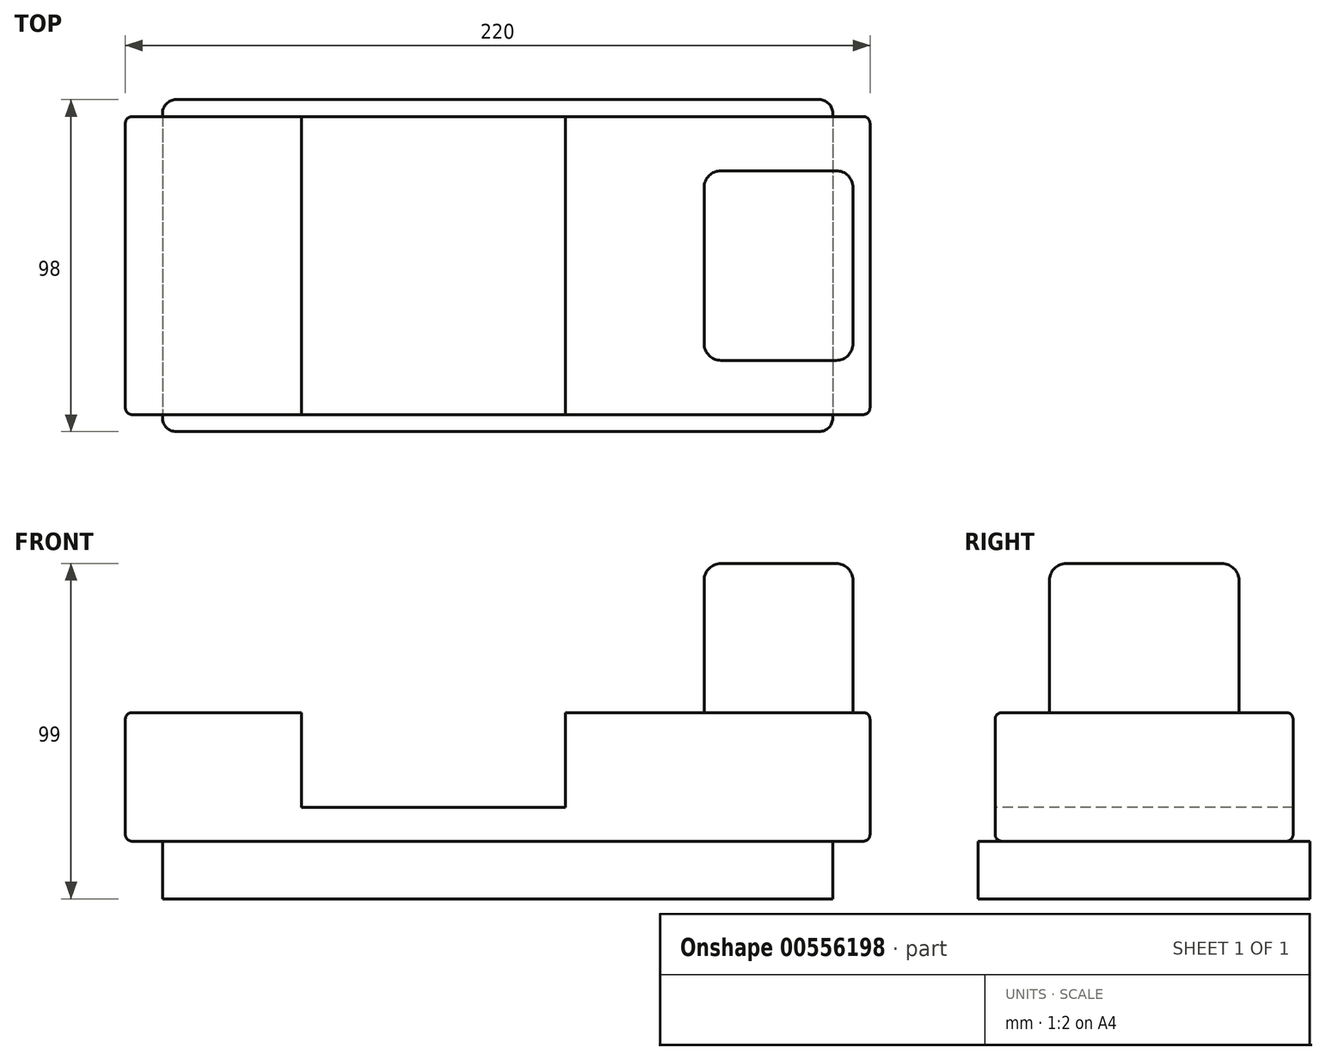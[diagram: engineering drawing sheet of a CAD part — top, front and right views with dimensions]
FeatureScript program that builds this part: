
annotation { "Feature Type Name" : "Feature", "Feature Type Description" : "" }
export const myFeature = defineFeature(function(context is Context, id is Id, definition is map)
    precondition{}
    {
        {
            assignVariable(context, id + "F0", {"name" : "cutdepth", "anyValue" : 28});
        }
        {
            var Q0;
            Q0=qCreatedBy(makeId("Top.planeOp"),FACE);
            var sketch = newSketch(context, id + "F1", { "sketchPlane" : qUnion([Q0])});
            skLineSegment(sketch, "E0.bottom", {"start": v(-89, 44.19) * mm, "end": v(109, 44.19) * mm});
            skLineSegment(sketch, "E0.top", {"start": v(-89, -53.81) * mm, "end": v(109, -53.81) * mm});
            skLineSegment(sketch, "E0.left", {"start": v(-89, 44.19) * mm, "end": v(-89, -53.81) * mm});
            skLineSegment(sketch, "E0.right", {"start": v(109, 44.19) * mm, "end": v(109, -53.81) * mm});
            skSolve(sketch);
        }
        {
            var Q0;
            Q0=qSketchRegion(id+"F1",true);
            extrude(context, id + "F2", {"entities" : qUnion([Q0]), "depth" : 17 * mm});
        }
        {
            var Q0;
            Q0=makeQuery(id+"F2.opExtrude","CAP_FACE",FACE,{"disambiguationData":[OSD([sQuery(id+"F1.wireOp",EDGE,"E0.bottom"),sQuery(id+"F1.wireOp",EDGE,"E0.top"),sQuery(id+"F1.wireOp",EDGE,"E0.left"),sQuery(id+"F1.wireOp",EDGE,"E0.right")])],"isStart":false});
            var sketch = newSketch(context, id + "F3", { "sketchPlane" : qUnion([Q0])});
            skLineSegment(sketch, "E1.bottom", {"start": v(-100, 39.19) * mm, "end": v(120, 39.19) * mm});
            skLineSegment(sketch, "E1.top", {"start": v(-100, -48.81) * mm, "end": v(120, -48.81) * mm});
            skLineSegment(sketch, "E1.left", {"start": v(-100, 39.19) * mm, "end": v(-100, -48.81) * mm});
            skLineSegment(sketch, "E1.right", {"start": v(120, 39.19) * mm, "end": v(120, -48.81) * mm});
            skLineSegment(sketch, "E2", {"start": v(10, -53.81) * mm, "end": v(10, 44.19) * mm, "construction": true});
            skLineSegment(sketch, "E3", {"start": v(-89, -4.81) * mm, "end": v(109, -4.81) * mm, "construction": true});
            skLineSegment(sketch, "E4", {"start": v(120, -48.81) * mm, "end": v(-100, 39.19) * mm, "construction": true});
            skLineSegment(sketch, "E5", {"start": v(-100, -48.81) * mm, "end": v(120, 39.19) * mm, "construction": true});
            skPoint(sketch, "E6", {"position": v(10, -4.81) * mm});
            skSolve(sketch);
        }
        {
            var Q0;
            Q0=qSketchRegion(id+"F3",true);
            extrude(context, id + "F4", {"entities" : qUnion([Q0]), "depth" : 38 * mm});
        }
        {
            var Q0;
            Q0=makeQuery(id+"F4.opExtrude","CAP_FACE",FACE,{"disambiguationData":[OSD([sQuery(id+"F3.wireOp",EDGE,"E1.bottom"),sQuery(id+"F3.wireOp",EDGE,"E1.top"),sQuery(id+"F3.wireOp",EDGE,"E1.left"),sQuery(id+"F3.wireOp",EDGE,"E1.right")])],"isStart":false});
            var sketch = newSketch(context, id + "F5", { "sketchPlane" : qUnion([Q0])});
            skLineSegment(sketch, "E7", {"start": v(93, 39.19) * mm, "end": v(93, -48.81) * mm, "construction": true});
            skPoint(sketch, "E8", {"position": v(93, -4.81) * mm});
            skLineSegment(sketch, "E9.bottom", {"start": v(115, 23.19) * mm, "end": v(71, 23.19) * mm});
            skLineSegment(sketch, "E9.top", {"start": v(115, -32.81) * mm, "end": v(71, -32.81) * mm});
            skLineSegment(sketch, "E9.left", {"start": v(115, 23.19) * mm, "end": v(115, -32.81) * mm});
            skLineSegment(sketch, "E9.right", {"start": v(71, 23.19) * mm, "end": v(71, -32.81) * mm});
            skLineSegment(sketch, "E10", {"start": v(115, 23.19) * mm, "end": v(71, -32.81) * mm, "construction": true});
            skSolve(sketch);
        }
        {
            var Q0;
            Q0=qSketchRegion(id+"F5",true);
            extrude(context, id + "F6", {"entities" : qUnion([Q0]), "depth" : 44 * mm});
        }
        {
            var Q0;
            Q0=makeQuery(id+"F4.opExtrude","CAP_FACE",FACE,{"disambiguationData":[OSD([sQuery(id+"F3.wireOp",EDGE,"E1.bottom"),sQuery(id+"F3.wireOp",EDGE,"E1.top"),sQuery(id+"F3.wireOp",EDGE,"E1.left"),sQuery(id+"F3.wireOp",EDGE,"E1.right")])],"isStart":false});
            var sketch = newSketch(context, id + "F7", { "sketchPlane" : qUnion([Q0])});
            skLineSegment(sketch, "E11.bottom", {"start": v(-48, 40.7) * mm, "end": v(30, 40.7) * mm});
            skLineSegment(sketch, "E11.top", {"start": v(-48, -49.3) * mm, "end": v(30, -49.3) * mm});
            skLineSegment(sketch, "E11.left", {"start": v(-48, 40.7) * mm, "end": v(-48, -49.3) * mm});
            skLineSegment(sketch, "E11.right", {"start": v(30, 40.7) * mm, "end": v(30, -49.3) * mm});
            skSolve(sketch);
        }
        {
            var Q0;
            Q0=qSketchRegion(id+"F7",true);
            extrude(context, id + "F8", {"entities" : qUnion([Q0]), "operationType" : NewBodyOperationType.REMOVE, "oppositeDirection" : true, "depth" : getVariable(context, 'cutdepth') * mm});
        }
        {
            var Q0;
            {var subQ0=sQuery(id+"F3.wireOp",EDGE,"E1.top");var subQ1=sQuery(id+"F3.wireOp",EDGE,"E1.left");Q0=makeQuery(id+"F8.boolean.opBoolean","SPLIT",EDGE,{"disambiguationData":[TD([makeQuery(id+"F4.opExtrude","SWEPT_FACE",FACE,{"disambiguationData":[OSD([subQ1])]})])],"derivedFrom":makeQuery(id+"F4.opExtrude","CAP_EDGE",EDGE,{"disambiguationData":[OSD([subQ0])],"isStart":false})});}
            var Q1;
            {var subQ0=sQuery(id+"F3.wireOp",EDGE,"E1.bottom");var subQ1=sQuery(id+"F3.wireOp",EDGE,"E1.left");Q1=makeQuery(id+"F8.boolean.opBoolean","SPLIT",EDGE,{"disambiguationData":[TD([makeQuery(id+"F4.opExtrude","SWEPT_FACE",FACE,{"disambiguationData":[OSD([subQ1])]})])],"derivedFrom":makeQuery(id+"F4.opExtrude","CAP_EDGE",EDGE,{"disambiguationData":[OSD([subQ0])],"isStart":false})});}
            var Q2;
            {var subQ0=sQuery(id+"F3.wireOp",EDGE,"E1.top");var subQ1=sQuery(id+"F3.wireOp",EDGE,"E1.right");Q2=makeQuery(id+"F8.boolean.opBoolean","SPLIT",EDGE,{"disambiguationData":[TD([makeQuery(id+"F4.opExtrude","SWEPT_FACE",FACE,{"disambiguationData":[OSD([subQ1])]})])],"derivedFrom":makeQuery(id+"F4.opExtrude","CAP_EDGE",EDGE,{"disambiguationData":[OSD([subQ0])],"isStart":false})});}
            var Q3;
            Q3=makeQuery(id+"F4.opExtrude","CAP_EDGE",EDGE,{"disambiguationData":[OSD([sQuery(id+"F3.wireOp",EDGE,"E1.top")])],"isStart":true});
            var Q4;
            {var subQ0=sQuery(id+"F3.wireOp",EDGE,"E1.bottom");var subQ1=sQuery(id+"F3.wireOp",EDGE,"E1.right");Q4=makeQuery(id+"F8.boolean.opBoolean","SPLIT",EDGE,{"disambiguationData":[TD([makeQuery(id+"F4.opExtrude","SWEPT_FACE",FACE,{"disambiguationData":[OSD([subQ1])]})])],"derivedFrom":makeQuery(id+"F4.opExtrude","CAP_EDGE",EDGE,{"disambiguationData":[OSD([subQ0])],"isStart":false})});}
            var Q5;
            Q5=makeQuery(id+"F4.opExtrude","CAP_EDGE",EDGE,{"disambiguationData":[OSD([sQuery(id+"F3.wireOp",EDGE,"E1.bottom")])],"isStart":true});
            var Q6;
            Q6=makeQuery(id+"F4.opExtrude","CAP_EDGE",EDGE,{"disambiguationData":[OSD([sQuery(id+"F3.wireOp",EDGE,"E1.left")])],"isStart":false});
            var Q7;
            Q7=makeQuery(id+"F4.opExtrude","SWEPT_EDGE",EDGE,{"disambiguationData":[OSD([sQuery(id+"F3.wireOp",EDGE,"E1.top"),sQuery(id+"F3.wireOp",EDGE,"E1.left")])]});
            var Q8;
            Q8=makeQuery(id+"F4.opExtrude","CAP_EDGE",EDGE,{"disambiguationData":[OSD([sQuery(id+"F3.wireOp",EDGE,"E1.left")])],"isStart":true});
            var Q9;
            Q9=makeQuery(id+"F4.opExtrude","SWEPT_EDGE",EDGE,{"disambiguationData":[OSD([sQuery(id+"F3.wireOp",EDGE,"E1.bottom"),sQuery(id+"F3.wireOp",EDGE,"E1.left")])]});
            var Q10;
            Q10=makeQuery(id+"F4.opExtrude","SWEPT_EDGE",EDGE,{"disambiguationData":[OSD([sQuery(id+"F3.wireOp",EDGE,"E1.top"),sQuery(id+"F3.wireOp",EDGE,"E1.right")])]});
            var Q11;
            Q11=makeQuery(id+"F4.opExtrude","CAP_EDGE",EDGE,{"disambiguationData":[OSD([sQuery(id+"F3.wireOp",EDGE,"E1.right")])],"isStart":false});
            var Q12;
            Q12=makeQuery(id+"F4.opExtrude","CAP_EDGE",EDGE,{"disambiguationData":[OSD([sQuery(id+"F3.wireOp",EDGE,"E1.right")])],"isStart":true});
            var Q13;
            Q13=makeQuery(id+"F4.opExtrude","SWEPT_EDGE",EDGE,{"disambiguationData":[OSD([sQuery(id+"F3.wireOp",EDGE,"E1.bottom"),sQuery(id+"F3.wireOp",EDGE,"E1.right")])]});
            var Q14;
            Q14=qNothing();
            fillet(context, id + "F9", {"entities" : qUnion([Q0, Q1, Q2, Q3, Q4, Q5, Q6, Q7, Q8, Q9, Q10, Q11, Q12, Q13, Q14]), "radius" : 2 * mm, "tangentPropagation" : true, "allowEdgeOverflow" : false});
        }
        {
            var Q0;
            Q0=makeQuery(id+"F2.opExtrude","SWEPT_EDGE",EDGE,{"disambiguationData":[OSD([sQuery(id+"F1.wireOp",EDGE,"E0.top"),sQuery(id+"F1.wireOp",EDGE,"E0.left")])]});
            var Q1;
            Q1=makeQuery(id+"F2.opExtrude","SWEPT_EDGE",EDGE,{"disambiguationData":[OSD([sQuery(id+"F1.wireOp",EDGE,"E0.top"),sQuery(id+"F1.wireOp",EDGE,"E0.right")])]});
            var Q2;
            Q2=makeQuery(id+"F2.opExtrude","SWEPT_EDGE",EDGE,{"disambiguationData":[OSD([sQuery(id+"F1.wireOp",EDGE,"E0.bottom"),sQuery(id+"F1.wireOp",EDGE,"E0.right")])]});
            var Q3;
            Q3=makeQuery(id+"F2.opExtrude","SWEPT_EDGE",EDGE,{"disambiguationData":[OSD([sQuery(id+"F1.wireOp",EDGE,"E0.bottom"),sQuery(id+"F1.wireOp",EDGE,"E0.left")])]});
            fillet(context, id + "F10", {"entities" : qUnion([Q0, Q1, Q2, Q3]), "radius" : 4 * mm, "tangentPropagation" : true, "allowEdgeOverflow" : false});
        }
        {
            var Q0;
            Q0=makeQuery(id+"F6.opExtrude","CAP_EDGE",EDGE,{"disambiguationData":[OSD([sQuery(id+"F5.wireOp",EDGE,"E9.top")])],"isStart":false});
            var Q1;
            Q1=makeQuery(id+"F6.opExtrude","CAP_EDGE",EDGE,{"disambiguationData":[OSD([sQuery(id+"F5.wireOp",EDGE,"E9.left")])],"isStart":false});
            var Q2;
            Q2=makeQuery(id+"F6.opExtrude","CAP_EDGE",EDGE,{"disambiguationData":[OSD([sQuery(id+"F5.wireOp",EDGE,"E9.bottom")])],"isStart":false});
            var Q3;
            Q3=makeQuery(id+"F6.opExtrude","CAP_EDGE",EDGE,{"disambiguationData":[OSD([sQuery(id+"F5.wireOp",EDGE,"E9.right")])],"isStart":false});
            var Q4;
            Q4=makeQuery(id+"F6.opExtrude","SWEPT_EDGE",EDGE,{"disambiguationData":[OSD([sQuery(id+"F5.wireOp",EDGE,"E9.top"),sQuery(id+"F5.wireOp",EDGE,"E9.left")])]});
            var Q5;
            Q5=makeQuery(id+"F6.opExtrude","SWEPT_EDGE",EDGE,{"disambiguationData":[OSD([sQuery(id+"F5.wireOp",EDGE,"E9.top"),sQuery(id+"F5.wireOp",EDGE,"E9.right")])]});
            var Q6;
            Q6=makeQuery(id+"F6.opExtrude","SWEPT_EDGE",EDGE,{"disambiguationData":[OSD([sQuery(id+"F5.wireOp",EDGE,"E9.bottom"),sQuery(id+"F5.wireOp",EDGE,"E9.left")])]});
            var Q7;
            Q7=makeQuery(id+"F6.opExtrude","SWEPT_EDGE",EDGE,{"disambiguationData":[OSD([sQuery(id+"F5.wireOp",EDGE,"E9.bottom"),sQuery(id+"F5.wireOp",EDGE,"E9.right")])]});
            fillet(context, id + "F11", {"entities" : qUnion([Q0, Q1, Q2, Q3, Q4, Q5, Q6, Q7]), "radius" : 5 * mm, "tangentPropagation" : true, "allowEdgeOverflow" : false});
        }
    });
